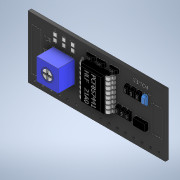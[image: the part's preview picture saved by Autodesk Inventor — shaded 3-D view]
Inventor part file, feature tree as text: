
AUTODESK INVENTOR PART (.ipt)
format: ipt  version: 2021 (Build 250183000, 183)  size: 2,601,984 bytes
history: native  units: mm
features: projected_geometry x29, sketch x16, extrude x14, chamfer x2, sweep x1, plane x1, mirror x1
ambient origin geometry x8: Origin, YZ Plane, XZ Plane, XY Plane, X Axis, Y Axis, Z Axis, Center Point
bodies: Solid1 (feature_tree)
feature tree (64):
  extrude  "Extrusion1"  Depth=0.65mm
  extrude  "Extrusion2"  Depth=0.65mm
  extrude  "Extrusion3"  Depth=2.54mm
  extrude  "Extrusion4"  Depth=2.54mm
  extrude  "Extrusion5"  Depth=2.54mm
  extrude  "Extrusion6"  Depth=2.54mm
  extrude  "Extrusion7"  Depth=2.54mm
  extrude  "Extrusion8"  Depth=2.54mm
  chamfer  "Chamfer1"  Distance=0.65mm
  extrude  "Extrusion9"  Depth=0.65mm
  chamfer  "Chamfer2"  Distance=0.65mm
  extrude  "Extrusion11"  Depth=0.65mm
  sweep  "Sweep1"
  plane  "Work Plane1"
  mirror  "Mirror1"
  extrude  "Extrusion12"  Depth=0.65mm
  extrude  "Extrusion13"  Depth=0.65mm
  extrude  "Extrusion14"  Depth=0.65mm
  extrude  "Extrusion15"  Depth=0.65mm
  sketch  "Sketch1"  dims[d53=38.1mm d54=0.65mm]
  sketch  "Sketch2"  dims[d55=0.65mm d56=0.65mm]
  sketch  "Sketch4"  dims[d57=0.65mm d58=2.54mm]
  projected_geometry  "Projected Loop1"
  sketch  "Sketch5"  dims[d59=2.54mm d60=2.54mm]
  projected_geometry  "Projected Loop2"
  sketch  "Sketch6"  dims[d61=2.54mm d62=2.54mm]
  sketch  "Sketch7"  dims[d63=2.54mm d64=2.54mm]
  projected_geometry  "Projected Loop3"
  sketch  "Sketch8"  dims[d65=2.54mm d66=2.54mm]
  projected_geometry  "Projected Loop4"
  projected_geometry  "Projected Loop5"
  projected_geometry  "Projected Loop6"
  projected_geometry  "Projected Loop7"
  sketch  "Sketch9"  dims[d67=2.54mm d68=2.54mm]
  projected_geometry  "Projected Loop8"
  projected_geometry  "Projected Loop9"
  projected_geometry  "Projected Loop10"
  projected_geometry  "Projected Loop11"
  projected_geometry  "Projected Loop12"
  projected_geometry  "Projected Loop13"
  projected_geometry  "Projected Loop14"
  projected_geometry  "Projected Loop15"
  projected_geometry  "Projected Loop16"
  projected_geometry  "Projected Loop17"
  projected_geometry  "Projected Loop18"
  sketch  "Sketch10"  dims[d69=2.54mm]
  projected_geometry  "Projected Loop19"
  sketch  "Sketch13"  dims[d70=2.54mm]
  sketch  "Sketch15"  dims[d71=2.54mm d72=0.65mm d73=0.65mm]
  projected_geometry  "Projected Loop21"
  sketch  "Sketch17"  dims[d74=0.65mm d75=0.65mm d76=0.65mm d77=0.65mm d78=0.65mm d79=0.65mm]
  sketch  "Sketch18"  dims[d80=0.65mm d81=0.65mm d82=0.65mm d83=0.65mm]
  projected_geometry  "Projected Loop22"
  projected_geometry  "Projected Loop23"
  projected_geometry  "Projected Loop24"
  sketch  "Sketch19"  dims[d84=0.65mm d85=0.65mm d86=0.65mm d87=0.65mm]
  projected_geometry  "Projected Loop25"
  projected_geometry  "Projected Loop26"
  projected_geometry  "Projected Loop27"
  sketch  "Sketch20"  dims[d88=0.65mm d89=0.65mm d90=0.65mm d91=0.65mm]
  sketch  "Sketch21"  dims[d92=0.65mm d93=0.65mm d94=0.65mm d95=0.65mm d96=0.65mm d97=0.65mm d98=0.65mm d99=0.65mm d100=1.95mm d101=1.95mm d102=1.5mm d103=1.5mm d104=19.0mm d105=19.0mm d106=1.0mm d107=0.0mm d111=7.0mm d112=0.1mm d114=3.0mm d117=0.1mm d121=0.1mm d123=2.5mm d124=4.0mm d125=0.1mm d126=1.0mm d127=3.0mm d128=1.5mm d129=0.9mm d131=0.1mm d132=3.0mm d133=1.5mm d134=0.1mm d135=3.0mm d136=1.5mm d137=0.1mm d138=3.0mm d139=1.5mm d140=0.1mm d141=3.0mm d142=1.5mm d143=0.1mm d144=3.0mm d145=1.5mm d146=0.1mm d147=3.0mm d148=1.5mm d149=0.1mm d150=3.0mm d151=1.5mm d152=0.1mm d153=3.0mm d154=1.5mm d155=0.1mm d156=3.0mm d157=1.5mm d158=0.1mm d159=18.0mm d160=3.5mm d161=7.4mm d162=10.5mm d163=0.1mm d164=3.0mm d165=1.5mm d166=0.1mm d167=3.0mm d168=1.5mm d169=0.1mm d170=3.0mm d171=1.5mm d172=0.1mm d173=0.1mm d174=0.0mm d175=0.1mm d176=5.1mm d177=0.0mm d178=3.0mm d179=1.0mm d180=0.0mm d181=3.5mm d182=3.7mm d183=0.25mm d184=0.0mm d185=0.5mm d186=0.5mm d187=1.01mm d188=0.0mm d189=0.1mm d190=0.1mm d191=0.1mm d192=0.2mm d193=0.2mm d194=0.1mm d195=0.0mm d196=0.1mm d197=0.1mm d198=0.1mm d199=0.1mm d200=0.1mm d201=0.1mm d202=0.1mm d203=0.1mm d204=0.1mm d205=0.1mm d206=0.1mm d207=0.1mm d208=1.0mm d209=0.0mm d210=0.5mm d211=2.0mm d212=45.0deg d213=0.1mm d214=2.5mm d215=0.0mm d216=0.5mm d217=2.0mm d218=45.0deg d238=0.1mm d239=0.0mm d240=10.3mm d257=10.3mm d276=0.5mm d277=0.5mm d278=0.5mm d279=0.5mm d280=0.5mm d281=0.5mm d282=0.5mm d283=0.5mm d308=0.25mm d309=0.25mm d310=0.0mm d311=0.0mm d312=-3.6mm d313=0.1mm d314=0.0mm d315=0.1mm d316=0.0mm d317=0.1mm d318=0.0mm d319=0.1mm d320=0.0mm]
  projected_geometry  "Projected Loop28"
  projected_geometry  "Projected Loop29"
  projected_geometry  "Projected Loop30"
